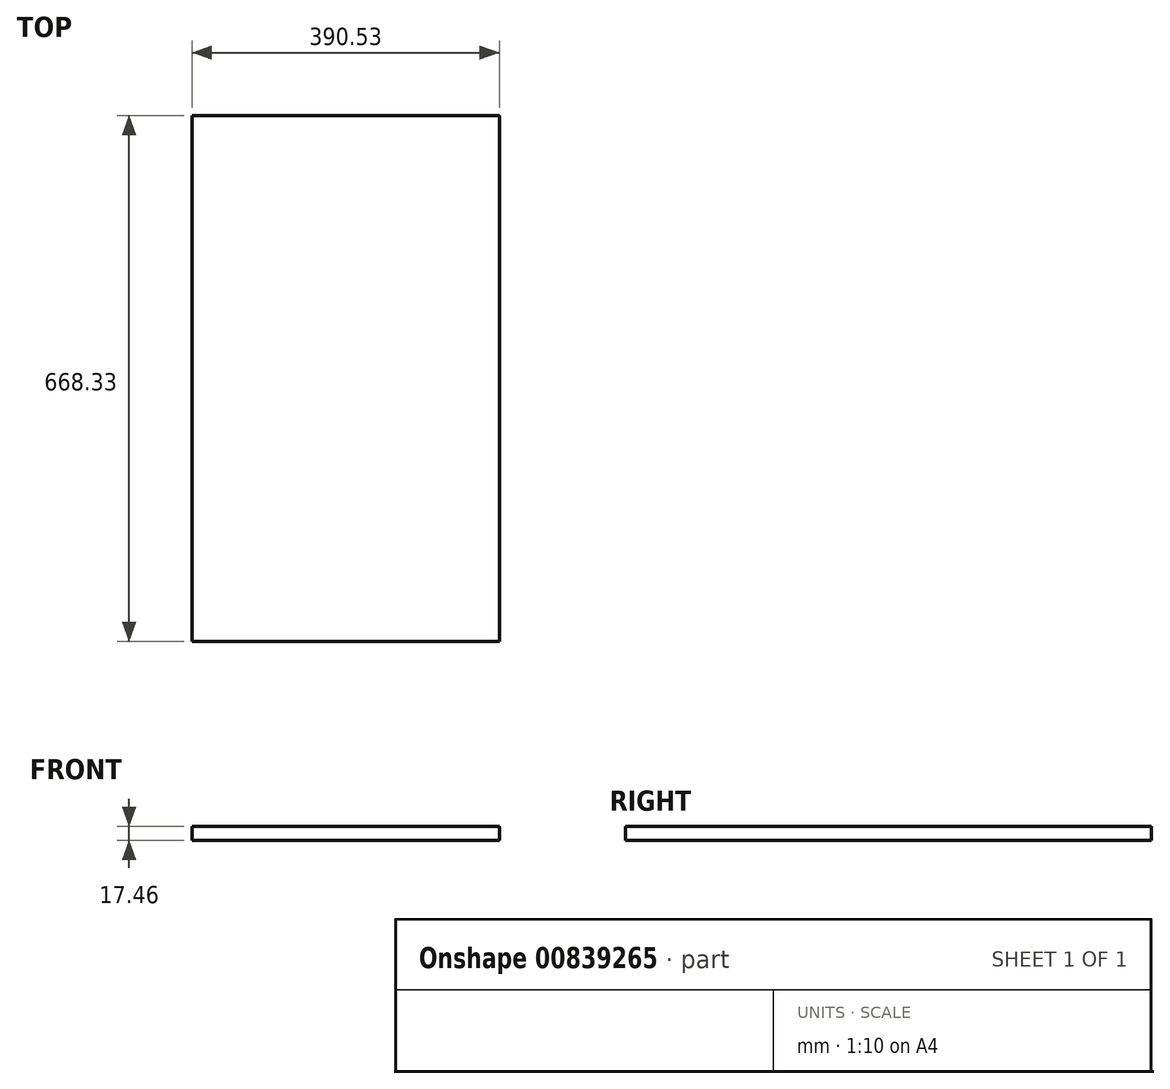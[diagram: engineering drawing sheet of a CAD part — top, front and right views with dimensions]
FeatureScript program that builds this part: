
annotation { "Feature Type Name" : "Feature", "Feature Type Description" : "" }
export const myFeature = defineFeature(function(context is Context, id is Id, definition is map)
    precondition{}
    {
        {
            var Q0;
            Q0=qCreatedBy(makeId("Top.planeOp"),FACE);
            var sketch = newSketch(context, id + "F0", { "sketchPlane" : qUnion([Q0])});
            skLineSegment(sketch, "E0.bottom", {"start": v(-257.17, 543.17) * mm, "end": v(133.36, 543.17) * mm});
            skLineSegment(sketch, "E0.top", {"start": v(-257.17, -125.16) * mm, "end": v(133.36, -125.16) * mm});
            skLineSegment(sketch, "E0.left", {"start": v(-257.17, 543.17) * mm, "end": v(-257.17, -125.16) * mm});
            skLineSegment(sketch, "E0.right", {"start": v(133.36, 543.17) * mm, "end": v(133.36, -125.16) * mm});
            skSolve(sketch);
        }
        {
            var Q0;
            Q0 = qSketchRegion(id + "F0", true);
            extrude(context, id + "F1", {"entities" : qUnion([Q0]), "depth" : 17.46 * mm, "offsetDistance" : 25.4 * mm});
        }
    });
